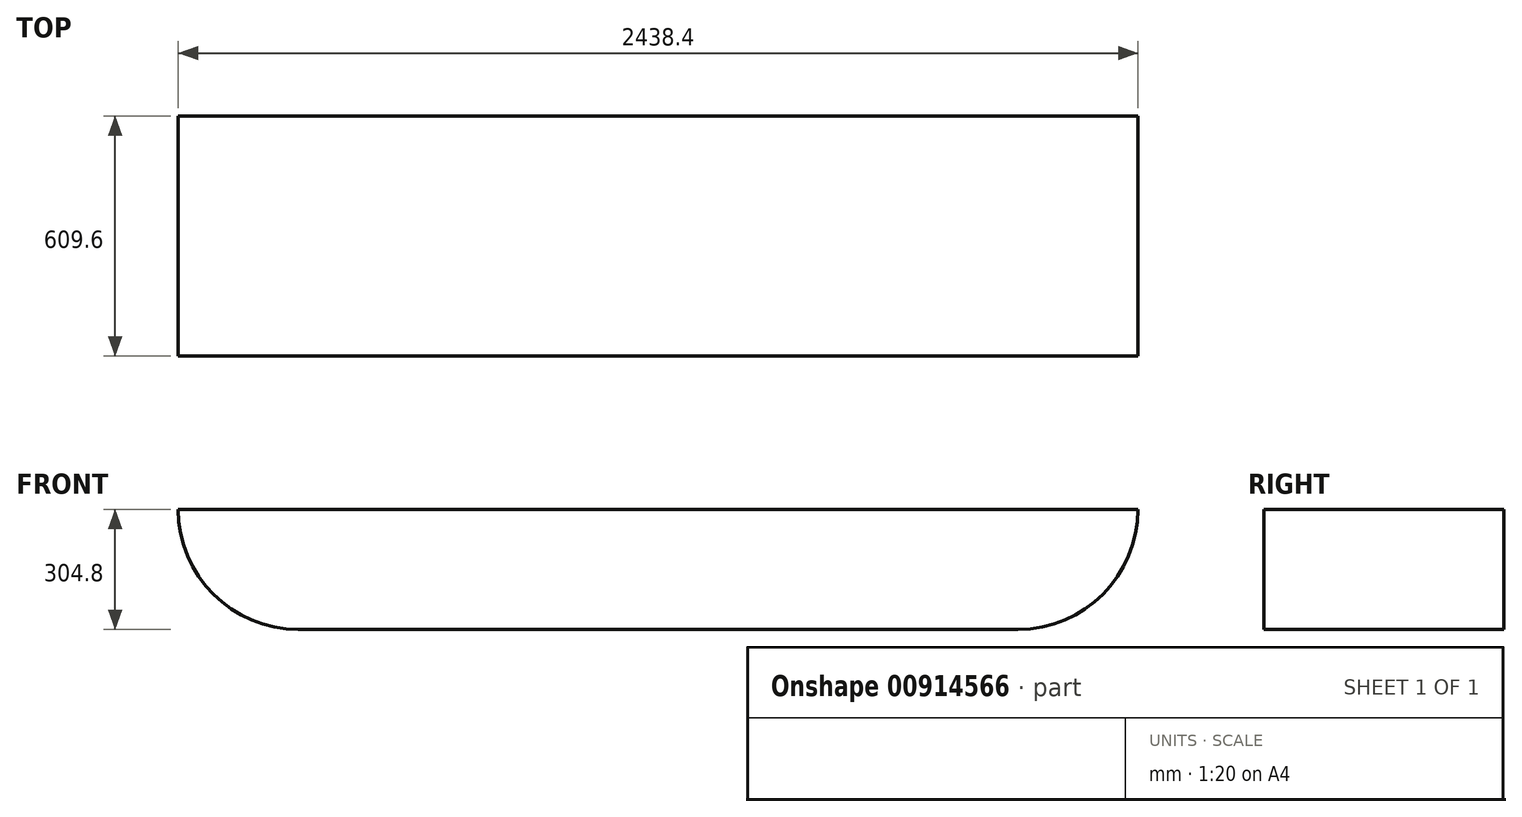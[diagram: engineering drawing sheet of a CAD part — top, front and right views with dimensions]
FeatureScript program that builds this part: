
annotation { "Feature Type Name" : "Feature", "Feature Type Description" : "" }
export const myFeature = defineFeature(function(context is Context, id is Id, definition is map)
    precondition{}
    {
        {
            var Q0;
            Q0=qCreatedBy(makeId("Front.planeOp"),FACE);
            var sketch = newSketch(context, id + "F0", { "sketchPlane" : qUnion([Q0])});
            skLineSegment(sketch, "E0.bottom", {"start": v(-914.4, 152.4) * mm, "end": v(914.4, 152.4) * mm});
            skLineSegment(sketch, "E0.top", {"start": v(-914.4, -152.4) * mm, "end": v(914.4, -152.4) * mm});
            skPoint(sketch, "E0.middle", {"position": v(0, 0) * mm});
            skArc(sketch, "E1", {"start": v(-914.4, -152.4) * mm, "mid": v(-1129.93, -63.13) * mm, "end": v(-1219.2, 152.4) * mm});
            skArc(sketch, "E2", {"start": v(914.4, -152.4) * mm, "mid": v(1129.93, -63.13) * mm, "end": v(1219.2, 152.4) * mm});
            skLineSegment(sketch, "E3", {"start": v(-1219.2, 152.4) * mm, "end": v(-914.4, 152.4) * mm});
            skLineSegment(sketch, "E4", {"start": v(1219.2, 152.4) * mm, "end": v(914.4, 152.4) * mm});
            skSolve(sketch);
        }
        {
            var Q0;
            Q0=makeQuery(id+"F0.imprint","IMPRINT",FACE,{"disambiguationData":[TD([[makeQuery(id+"F0.imprint","IMPRINT",EDGE,{"derivedFrom":sQuery(id+"F0.wireOp",EDGE,"E0.bottom")}),-1.0]])]});
            extrude(context, id + "F1", {"entities" : qUnion([Q0]), "depth" : 609.6 * mm, "offsetDistance" : 25.4 * mm});
        }
    });
